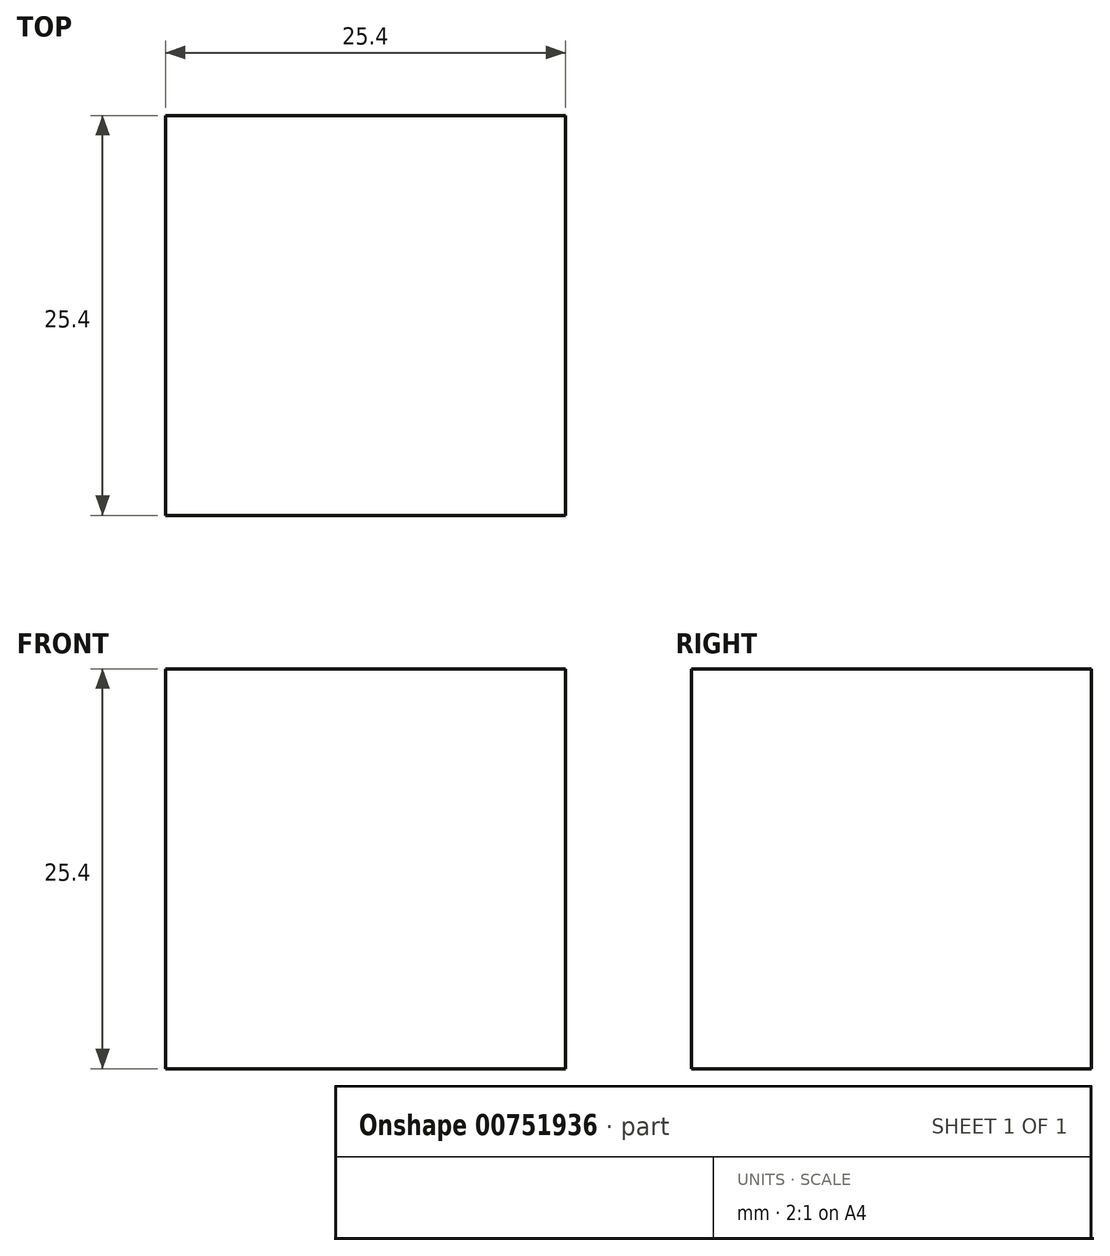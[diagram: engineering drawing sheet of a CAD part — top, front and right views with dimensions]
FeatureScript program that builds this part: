
annotation { "Feature Type Name" : "Feature", "Feature Type Description" : "" }
export const myFeature = defineFeature(function(context is Context, id is Id, definition is map)
    precondition{}
    {
        {
            var Q0;
            Q0=qCreatedBy(makeId("Front.planeOp"),FACE);
            var sketch = newSketch(context, id + "F0", { "sketchPlane" : qUnion([Q0])});
            skLineSegment(sketch, "E0.bottom", {"start": v(0, 0) * mm, "end": v(25.4, 0) * mm});
            skLineSegment(sketch, "E0.top", {"start": v(0, 25.4) * mm, "end": v(25.4, 25.4) * mm});
            skLineSegment(sketch, "E0.left", {"start": v(0, 0) * mm, "end": v(0, 25.4) * mm});
            skLineSegment(sketch, "E0.right", {"start": v(25.4, 0) * mm, "end": v(25.4, 25.4) * mm});
            skSolve(sketch);
        }
        {
            var Q0;
            Q0=makeQuery(id+"F0.imprint","IMPRINT",FACE,{"disambiguationData":[TD([[makeQuery(id+"F0.imprint","IMPRINT",EDGE,{"derivedFrom":sQuery(id+"F0.wireOp",EDGE,"E0.bottom")}),1.0]])]});
            extrude(context, id + "F1", {"entities" : qUnion([Q0]), "depth" : 25.4 * mm, "offsetDistance" : 25.4 * mm});
        }
    });
